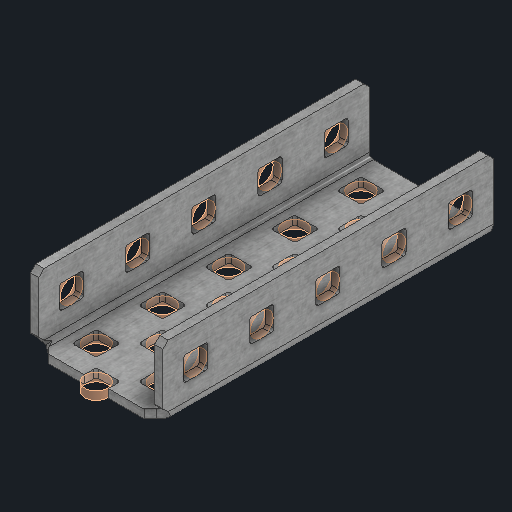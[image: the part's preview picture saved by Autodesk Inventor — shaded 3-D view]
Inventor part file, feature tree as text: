
AUTODESK INVENTOR PART (.ipt)
format: ipt  version: 2025 (Build 290162000, 162)  size: 653,824 bytes
history: native  units: in
note: dims shown in document units (in); Inventor stores cm internally (conversion verified against a paired STEP export)
features: other x56, sketch x5, sheet_metal_op x1
ambient origin geometry x8: Origin, YZ Plane, XZ Plane, XY Plane, X Axis, Y Axis, Z Axis, Center Point
bodies: Solid1 (feature_tree)
feature tree (62):
  other  "Alu C 1x2x1x5.ipt"
  other  "Solid1::Alu C 1x2x1x5.ipt"
  other  "TaggingFeature1"
  sketch  "Sketch1"  dims[d0=0.3937in]
  sketch  "Sketch2"  dims[d1=0.0625in]
  sketch  "Sketch3"
  other  "Flange Pattern Sketch"
  sketch  "Sketch9"
  sheet_metal_op  "Body Pattern Sketch"
  other  "Arc Length"
  sketch  "Sketch14"
  other  "Flange Pattern Plane"
  other  "Srf1"
  other  "Srf2"
  other  "Srf3"
  other  "Srf4"
  other  "Srf5"
  other  "Srf6"
  other  "Srf7"
  other  "Srf8"
  other  "Srf9"
  other  "Srf10"
  other  "Srf11"
  other  "Srf12"
  other  "Srf13"
  other  "Srf14"
  other  "Srf15"
  other  "Srf16"
  other  "Srf17"
  other  "Srf18"
  other  "Srf19"
  other  "Srf20"
  other  "Srf21"
  other  "Srf22"
  other  "Srf23"
  other  "Srf24"
  other  "Srf25"
  other  "Srf1::Derived"
  other  "Srf2::Derived"
  other  "Srf823::Derived"
  other  "Srf824::Derived"
  other  "Srf825::Derived"
  other  "Srf826::Derived"
  other  "Srf827::Derived"
  other  "Srf828::Derived"
  other  "Srf829::Derived"
  other  "Srf922::Derived"
  other  "Srf91::Derived"
  other  "Srf92::Derived"
  other  "Srf856::Derived"
  other  "Srf857::Derived"
  other  "Srf858::Derived"
  other  "Srf859::Derived"
  other  "Srf860::Derived"
  other  "Srf861::Derived"
  other  "Srf862::Derived"
  other  "Srf959::Derived"
  other  "Srf786::Derived"
  other  "Srf889::Derived"
  other  "Srf890::Derived"
  other  "Srf891::Derived"
  other  "Srf892::Derived"
